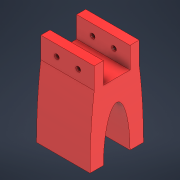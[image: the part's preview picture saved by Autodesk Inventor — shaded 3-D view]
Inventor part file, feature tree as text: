
AUTODESK INVENTOR PART (.ipt)
format: ipt  version: 2022 (Build 260153000, 153)  size: 187,392 bytes
history: native  units: mm
features: extrude x4, sketch x4, projected_geometry x4
ambient origin geometry x8: Origin, YZ Plane, XZ Plane, XY Plane, X Axis, Y Axis, Z Axis, Center Point
bodies: Solid1 (feature_tree)
feature tree (12):
  extrude  "Extrusion1"  Depth=50.0mm
  extrude  "Extrusion3"  Depth=45.0mm
  extrude  "Extrusion4"  Depth=120.0mm
  extrude  "Extrusion5"  Depth=8.514834mm
  sketch  "Sketch1"  dims[d7=50.0mm d8=0.0mm d18=50.0mm]
  sketch  "Sketch3"  dims[d22=25.0mm d23=45.0mm]
  projected_geometry  "Projected Loop5"
  sketch  "Sketch4"  dims[d24=64.999994mm d25=120.0mm]
  projected_geometry  "Projected Loop6"
  sketch  "Sketch5"  dims[d26=25.0mm d27=8.514834mm d28=8.514834mm d29=20.0mm d30=0.0mm d31=4.5mm d32=4.5mm d33=20.0mm d34=15.0mm d35=15.0mm d36=0.0mm d37=0.0mm d38=38.6mm d39=38.6mm d40=7.0mm d41=7.0mm d42=7.0mm d43=7.0mm d44=10.0mm d45=0.0mm]
  projected_geometry  "Projected Loop7"
  projected_geometry  "Projected Loop8"
